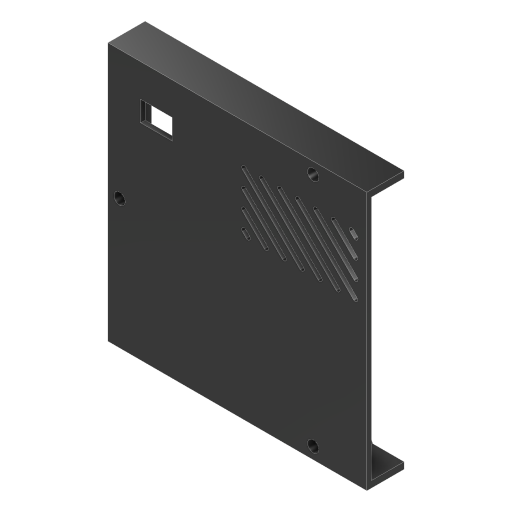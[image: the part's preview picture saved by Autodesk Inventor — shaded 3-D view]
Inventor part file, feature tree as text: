
AUTODESK INVENTOR PART (.ipt)
format: ipt  version: 2023 (Build 270158000, 158)  size: 780,800 bytes
history: native  units: mm
features: sketch x8, projected_geometry x8, extrude x5, hole x3, other x1
ambient origin geometry x8: Origin, YZ Plane, XZ Plane, XY Plane, X Axis, Y Axis, Z Axis, Center Point
bodies: Body1 (feature_tree)
feature tree (25):
  other  "Těleso1"
  extrude  "Vysunutí1"  Depth=158.75mm
  extrude  "Vysunutí2"  Depth=158.5mm
  extrude  "Vysunutí3"  Depth=83.5mm
  hole  "Díra1"  [1 undecoded]
  hole  "Díra2"  [1 undecoded]
  extrude  "Vysunutí4"  Depth=4.0mm
  extrude  "Vysunutí5"  Depth=4.0mm
  hole  "Díra3"  [1 undecoded]
  sketch  "Náčrt1"
  sketch  "Náčrt2"
  projected_geometry  "Promítnutá smyčka1"
  sketch  "Náčrt3"
  projected_geometry  "Promítnutá smyčka2"
  sketch  "Náčrt4"
  projected_geometry  "Promítnutá smyčka3"
  sketch  "Náčrt5"
  sketch  "Náčrt6"
  projected_geometry  "Promítnutá smyčka4"
  sketch  "Náčrt7"
  sketch  "Náčrt8"
  projected_geometry  "Promítnutá smyčka5"
  projected_geometry  "Promítnutá smyčka6"
  projected_geometry  "Promítnutá smyčka7"
  projected_geometry  "Promítnutá smyčka8"
note: 3 required parameter values undecoded (feature->parameter linkage not recoverable at this tier; creation-order binding heuristic only, values carry confidence <= 0.55)
